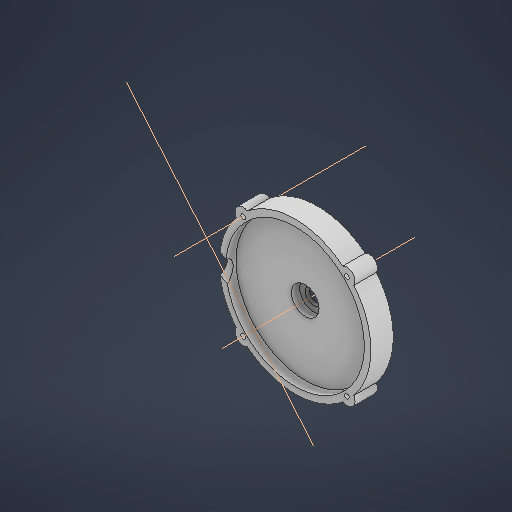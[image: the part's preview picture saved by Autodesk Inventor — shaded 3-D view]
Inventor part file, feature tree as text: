
AUTODESK INVENTOR PART (.ipt)
format: ipt  version: 2025.3 (Build 293356030, 356C)  size: 281,088 bytes
history: native  units: mm
features: sketch x6, extrude x5, other x4, plane x2
ambient origin geometry x8: Origin, YZ Plane, XZ Plane, XY Plane, X Axis, Y Axis, Z Axis, Center Point
bodies: Solid1 (feature_tree)
feature tree (17):
  sketch  "Sketch1"  dims[d1=40.0mm]
  extrude  "Extrusion1"  Depth=3.75mm TaperAngle=0.0deg
  extrude  "Extrusion2"  TaperAngle=105.0deg  [1 undecoded]
  extrude  "Extrusion3"  Depth=10.65mm
  sketch  "Sketch2"  dims[d14=10.0mm d15=0.0mm d18=105.0deg]
  plane  "Work Plane1"
  sketch  "Sketch3"  dims[d19=30.0deg d20=10.65mm]
  plane  "Work Plane2"
  extrude  "Extrusion5"  Depth=93.0mm
  other  "Work Axis1"
  other  "Work Axis2"
  other  "Work Axis3"
  other  "Work Axis4"
  extrude  "Extrusion6"  Depth=0.5mm
  sketch  "Sketch Circular Pattern1"  dims[d2=10.0mm d3=16.9mm d4=85.0mm d5=90.0mm d6=2.9mm d7=5.0mm d8=360.0deg d10=3.75mm d11=0.0mm d12=7.5mm d13=0.0mm]
  sketch  "Sketch4"  dims[d21=20.0mm d22=0.0mm d24=93.0mm]
  sketch  "Sketch5"  dims[d25=2.5mm d26=0.0mm d23=0.5mm]
note: 1 required parameter value undecoded (feature->parameter linkage not recoverable at this tier; creation-order binding heuristic only, values carry confidence <= 0.55)
